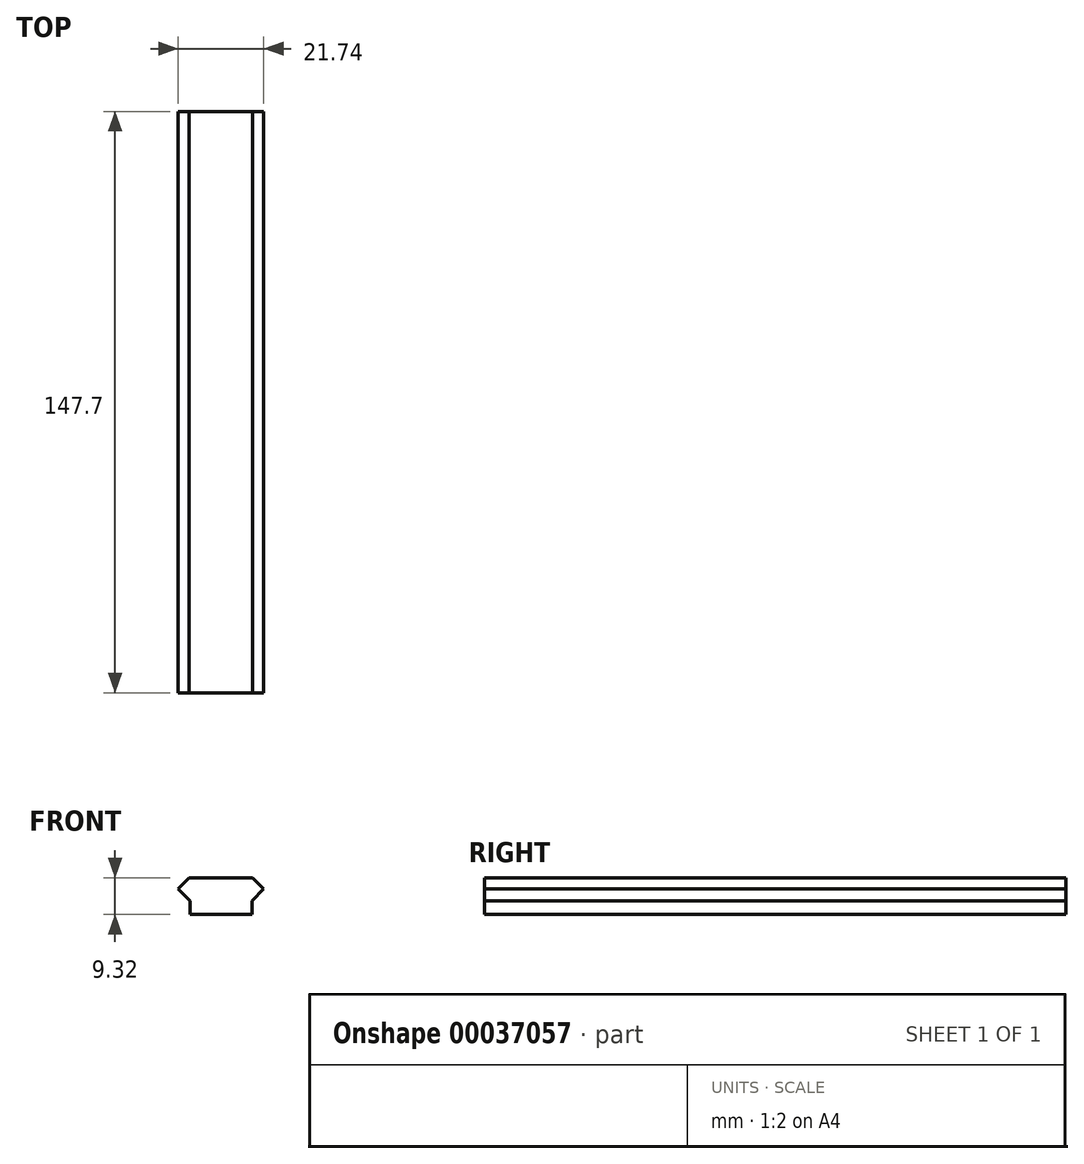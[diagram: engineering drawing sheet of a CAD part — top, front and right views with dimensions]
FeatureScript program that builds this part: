
annotation { "Feature Type Name" : "Feature", "Feature Type Description" : "" }
export const myFeature = defineFeature(function(context is Context, id is Id, definition is map)
    precondition{}
    {
        {
            var Q0;
            Q0=qCreatedBy(makeId("Front.planeOp"),FACE);
            var sketch = newSketch(context, id + "F0", { "sketchPlane" : qUnion([Q0])});
            skLineSegment(sketch, "E0.rect.bottom", {"start": v(-9.5, -1.37) * mm, "end": v(9.5, -1.37) * mm});
            skLineSegment(sketch, "E0.rect.top", {"start": v(-9.5, 1.37) * mm, "end": v(9.5, 1.37) * mm});
            skLineSegment(sketch, "E0.rect.left", {"start": v(-9.5, -1.37) * mm, "end": v(-9.5, 1.37) * mm});
            skLineSegment(sketch, "E0.rect.right", {"start": v(9.5, -1.37) * mm, "end": v(9.5, 1.37) * mm});
            skPoint(sketch, "E0.rect.middle", {"position": v(0, 0) * mm});
            skLineSegment(sketch, "E1", {"start": v(0, -1.37) * mm, "end": v(0, 2.8) * mm, "construction": true});
            skLineSegment(sketch, "E2", {"start": v(0, -1.37) * mm, "end": v(10.6, -1.37) * mm, "construction": true});
            skLineSegment(sketch, "E3.bottom", {"start": v(10.6, -1.37) * mm, "end": v(-10.6, -1.37) * mm, "construction": true});
            skLineSegment(sketch, "E3.top", {"start": v(10.6, 1.37) * mm, "end": v(-10.6, 1.37) * mm, "construction": true});
            skLineSegment(sketch, "E3.left", {"start": v(10.6, -1.37) * mm, "end": v(10.6, 1.37) * mm, "construction": true});
            skLineSegment(sketch, "E3.right", {"start": v(-10.6, -1.37) * mm, "end": v(-10.6, 1.37) * mm, "construction": true});
            skLineSegment(sketch, "E4", {"start": v(0, 2.8) * mm, "end": v(14.87, 2.8) * mm, "construction": true});
            skLineSegment(sketch, "E5", {"start": v(9.5, 1.37) * mm, "end": v(7.12, 3.75) * mm, "construction": true});
            skLineSegment(sketch, "E6", {"start": v(9.5, 1.37) * mm, "end": v(10.87, 0) * mm});
            skLineSegment(sketch, "E7", {"start": v(9.5, -1.37) * mm, "end": v(10.87, 0) * mm});
            skLineSegment(sketch, "E8", {"start": v(9.5, -1.37) * mm, "end": v(7.84, -3.04) * mm});
            skLineSegment(sketch, "E9", {"start": v(0, -1.37) * mm, "end": v(0, -6.53) * mm});
            skLineSegment(sketch, "E10", {"start": v(0, -6.53) * mm, "end": v(7.84, -6.53) * mm});
            skLineSegment(sketch, "E11", {"start": v(0, 2.8) * mm, "end": v(8.08, 2.8) * mm});
            skLineSegment(sketch, "E12", {"start": v(8.08, 2.8) * mm, "end": v(9.5, 1.37) * mm});
            skLineSegment(sketch, "E13", {"start": v(0, 2.8) * mm, "end": v(0, -1.37) * mm});
            skLineSegment(sketch, "E14", {"start": v(7.84, -6.53) * mm, "end": v(7.84, -3.04) * mm});
            skLineSegment(sketch, "E15.MirrorCS", {"start": v(-7.84, -6.53) * mm, "end": v(-7.84, -3.04) * mm});
            skLineSegment(sketch, "E16.MirrorCS", {"start": v(0, -6.53) * mm, "end": v(-7.84, -6.53) * mm});
            skLineSegment(sketch, "E17.MirrorCS", {"start": v(-9.5, -1.37) * mm, "end": v(-7.84, -3.04) * mm});
            skLineSegment(sketch, "E18.MirrorCS", {"start": v(-9.5, -1.37) * mm, "end": v(-10.87, 0) * mm});
            skLineSegment(sketch, "E19.MirrorCS", {"start": v(-8.08, 2.8) * mm, "end": v(-9.5, 1.37) * mm});
            skLineSegment(sketch, "E20.MirrorCS", {"start": v(-9.5, 1.37) * mm, "end": v(-10.87, 0) * mm});
            skLineSegment(sketch, "E21.MirrorCS", {"start": v(0, 2.8) * mm, "end": v(-8.08, 2.8) * mm});
            skPoint(sketch, "E22.orphan", {"position": v(6.1, -4.76) * mm});
            skPoint(sketch, "E23.orphan", {"position": v(7.84, -1.37) * mm});
            skPoint(sketch, "E24.orphan", {"position": v(12.12, 1.25) * mm});
            skPoint(sketch, "E25.orphan", {"position": v(11.8, -0.93) * mm});
            skPoint(sketch, "E26.orphan", {"position": v(-6.1, -4.76) * mm});
            skPoint(sketch, "E27.orphan", {"position": v(-7.84, -1.37) * mm});
            skPoint(sketch, "E28.orphan", {"position": v(-12.12, 1.25) * mm});
            skPoint(sketch, "E29.orphan", {"position": v(-11.8, -0.93) * mm});
            skSolve(sketch);
        }
        {
            var Q0;
            {var subQ1=sQuery(id+"F0.wireOp",EDGE,"E8");Q0=makeQuery(id+"F0.imprint","IMPRINT",FACE,{"disambiguationData":[TD([[makeQuery(id+"F0.imprint","IMPRINT",EDGE,{"derivedFrom":subQ1}),-1.0]])]});}
            var Q1;
            {var subQ1=sQuery(id+"F0.wireOp",EDGE,"E9");Q1=makeQuery(id+"F0.imprint","IMPRINT",FACE,{"disambiguationData":[TD([[makeQuery(id+"F0.imprint","IMPRINT",EDGE,{"derivedFrom":subQ1}),-1.0]])]});}
            var Q2;
            {var subQ5=sQuery(id+"F0.wireOp",EDGE,"E0.rect.right");Q2=makeQuery(id+"F0.imprint","IMPRINT",FACE,{"disambiguationData":[TD([[makeQuery(id+"F0.imprint","IMPRINT",EDGE,{"derivedFrom":subQ5}),1.0]])]});}
            var Q3;
            Q3=makeQuery(id+"F0.imprint","IMPRINT",FACE,{"disambiguationData":[TD([[makeQuery(id+"F0.imprint","IMPRINT",EDGE,{"derivedFrom":sQuery(id+"F0.wireOp",EDGE,"E0.rect.right")}),-1.0]])]});
            var Q4;
            {var subQ3=sQuery(id+"F0.wireOp",EDGE,"E11");Q4=makeQuery(id+"F0.imprint","IMPRINT",FACE,{"disambiguationData":[TD([[makeQuery(id+"F0.imprint","IMPRINT",EDGE,{"derivedFrom":subQ3}),-1.0]])]});}
            var Q5;
            {var subQ1=sQuery(id+"F0.wireOp",EDGE,"E19.MirrorCS");Q5=makeQuery(id+"F0.imprint","IMPRINT",FACE,{"disambiguationData":[TD([[makeQuery(id+"F0.imprint","IMPRINT",EDGE,{"derivedFrom":subQ1}),1.0]])]});}
            var Q6;
            {var subQ5=sQuery(id+"F0.wireOp",EDGE,"E0.rect.left");Q6=makeQuery(id+"F0.imprint","IMPRINT",FACE,{"disambiguationData":[TD([[makeQuery(id+"F0.imprint","IMPRINT",EDGE,{"derivedFrom":subQ5}),-1.0]])]});}
            var Q7;
            Q7=makeQuery(id+"F0.imprint","IMPRINT",FACE,{"disambiguationData":[TD([[makeQuery(id+"F0.imprint","IMPRINT",EDGE,{"derivedFrom":sQuery(id+"F0.wireOp",EDGE,"E0.rect.left")}),1.0]])]});
            extrude(context, id + "F1", {"entities" : qUnion([Q0, Q1, Q2, Q3, Q4, Q5, Q6, Q7]), "depth" : 147.7 * mm});
        }
    });
